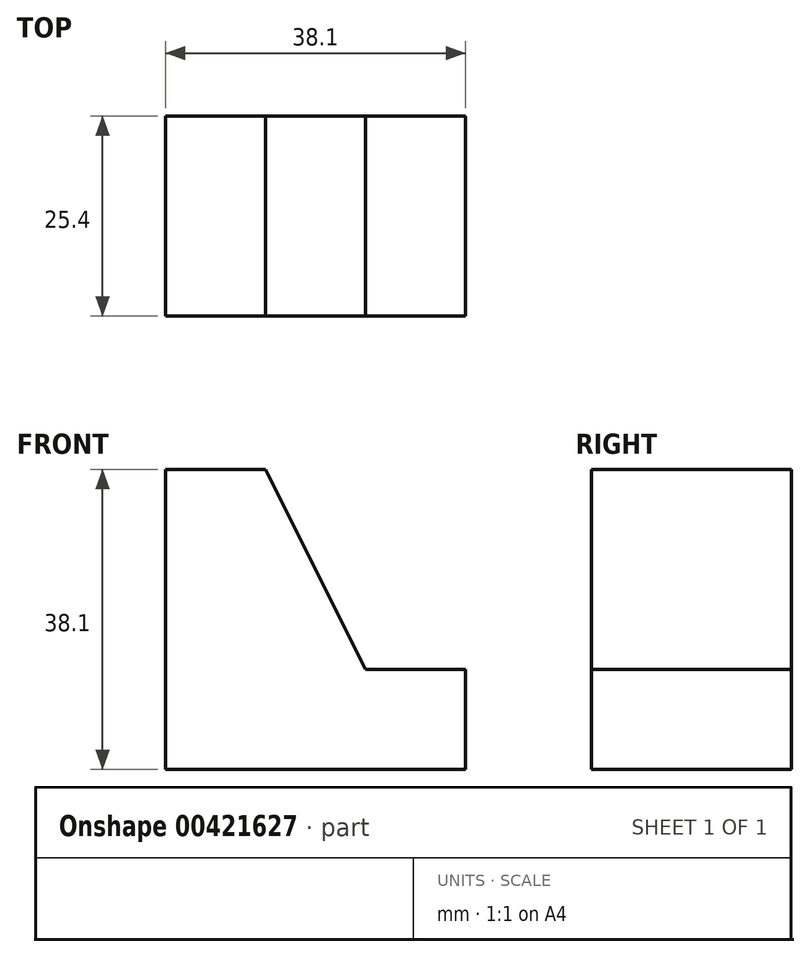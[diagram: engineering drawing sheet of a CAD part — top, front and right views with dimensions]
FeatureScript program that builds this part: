
annotation { "Feature Type Name" : "Feature", "Feature Type Description" : "" }
export const myFeature = defineFeature(function(context is Context, id is Id, definition is map)
    precondition{}
    {
        {
            var Q0;
            Q0=qCreatedBy(makeId("Front.planeOp"),FACE);
            var sketch = newSketch(context, id + "F0", { "sketchPlane" : qUnion([Q0])});
            skLineSegment(sketch, "E0", {"start": v(0, 0) * mm, "end": v(38.1, 0) * mm});
            skLineSegment(sketch, "E1", {"start": v(38.1, 0) * mm, "end": v(38.1, 12.7) * mm});
            skLineSegment(sketch, "E2", {"start": v(0, 0) * mm, "end": v(0, 38.1) * mm});
            skLineSegment(sketch, "E3", {"start": v(0, 38.1) * mm, "end": v(12.7, 38.1) * mm});
            skLineSegment(sketch, "E4", {"start": v(38.1, 12.7) * mm, "end": v(25.4, 12.7) * mm});
            skLineSegment(sketch, "E5", {"start": v(12.7, 38.1) * mm, "end": v(25.4, 12.7) * mm});
            skSolve(sketch);
        }
        {
            var Q0;
            Q0 = qSketchRegion(id + "F0", true);
            extrude(context, id + "F1", {"entities" : qUnion([Q0]), "depth" : 25.4 * mm});
        }
    });
